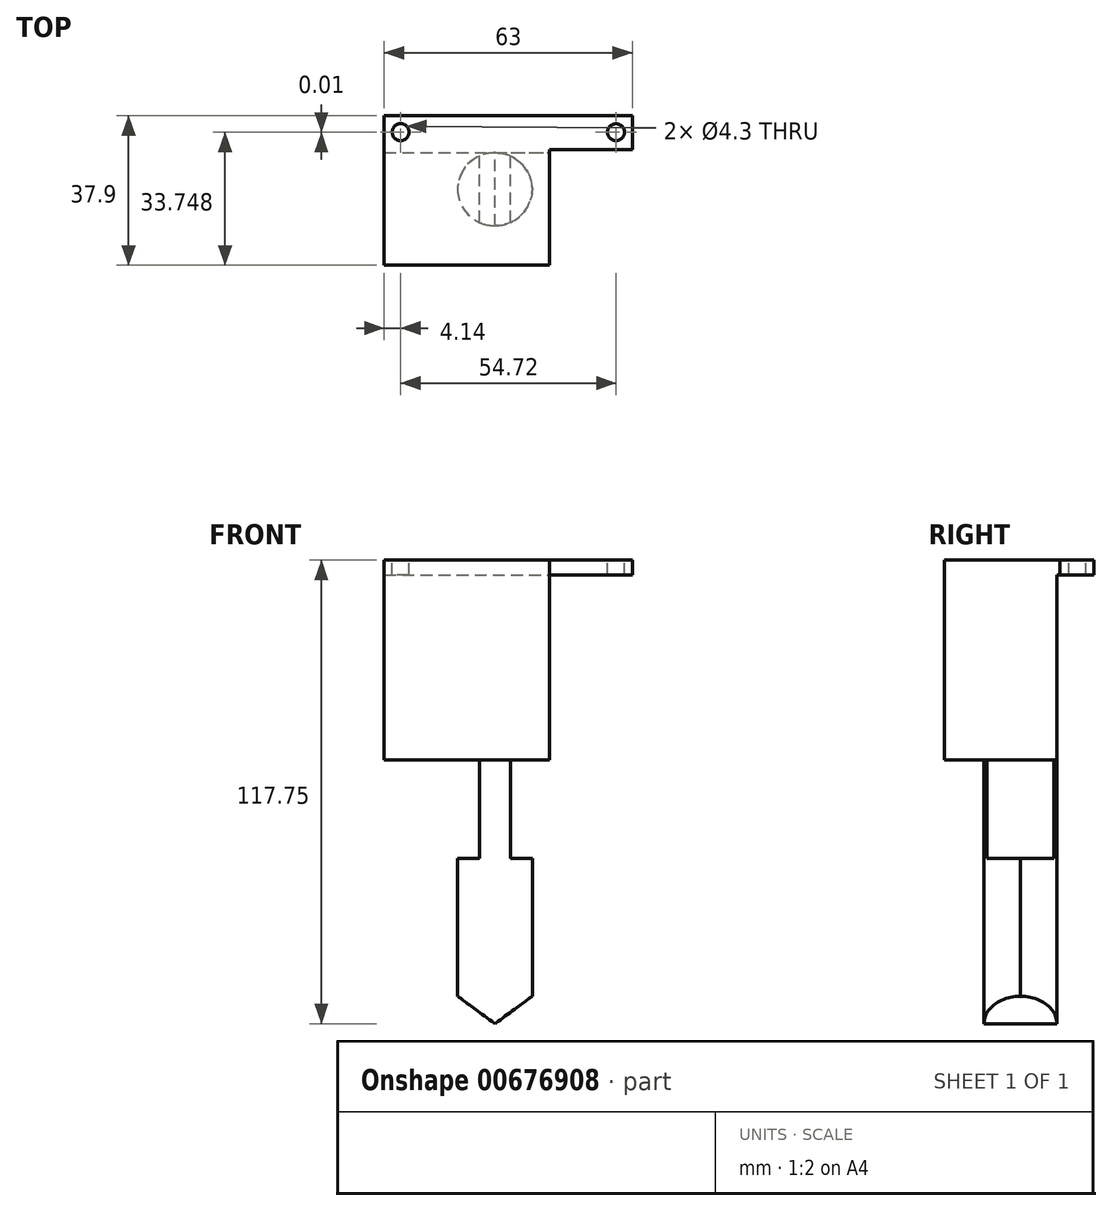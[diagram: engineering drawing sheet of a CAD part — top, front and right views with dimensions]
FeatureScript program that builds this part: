
annotation { "Feature Type Name" : "Feature", "Feature Type Description" : "" }
export const myFeature = defineFeature(function(context is Context, id is Id, definition is map)
    precondition{}
    {
        {
            var Q0;
            Q0=qCreatedBy(makeId("Front.planeOp"),FACE);
            var sketch = newSketch(context, id + "F0", { "sketchPlane" : qUnion([Q0])});
            skLineSegment(sketch, "E0", {"start": v(9.5, 7) * mm, "end": v(0, 0) * mm});
            skLineSegment(sketch, "E1", {"start": v(9.5, 7) * mm, "end": v(9.5, 42) * mm});
            skLineSegment(sketch, "E2", {"start": v(9.5, 42) * mm, "end": v(3.9, 42) * mm});
            skLineSegment(sketch, "E3", {"start": v(3.9, 42) * mm, "end": v(3.9, 67) * mm});
            skLineSegment(sketch, "E4", {"start": v(3.9, 67) * mm, "end": v(13.9, 67) * mm});
            skLineSegment(sketch, "E5", {"start": v(13.9, 67) * mm, "end": v(13.9, 114) * mm});
            skLineSegment(sketch, "E6", {"start": v(13.9, 114) * mm, "end": v(34.9, 114) * mm});
            skLineSegment(sketch, "E7", {"start": v(34.9, 114) * mm, "end": v(34.9, 117.75) * mm});
            skLineSegment(sketch, "E8", {"start": v(34.9, 117.75) * mm, "end": v(-28.1, 117.75) * mm});
            skLineSegment(sketch, "E9", {"start": v(-28.1, 117.75) * mm, "end": v(-28.1, 114) * mm});
            skLineSegment(sketch, "E10", {"start": v(-28.1, 114) * mm, "end": v(-28.1, 67) * mm});
            skLineSegment(sketch, "E11", {"start": v(-28.1, 67) * mm, "end": v(-3.9, 67) * mm});
            skLineSegment(sketch, "E12", {"start": v(-3.9, 67) * mm, "end": v(-3.9, 42) * mm});
            skLineSegment(sketch, "E13", {"start": v(-3.9, 42) * mm, "end": v(-9.5, 42) * mm});
            skLineSegment(sketch, "E14", {"start": v(-9.5, 42) * mm, "end": v(-9.5, 7) * mm});
            skLineSegment(sketch, "E15", {"start": v(-9.5, 7) * mm, "end": v(0, 0) * mm});
            skSolve(sketch);
        }
        {
            var Q0;
            Q0=makeQuery(id+"F0.imprint","IMPRINT",FACE,{"disambiguationData":[TD([[makeQuery(id+"F0.imprint","IMPRINT",EDGE,{"derivedFrom":sQuery(id+"F0.wireOp",EDGE,"E0")}),-1.0]])]});
            extrude(context, id + "F1", {"entities" : qUnion([Q0]), "depth" : 18.5 / 2 * mm, "offsetDistance" : 25.4 * mm, "hasSecondDirection" : true, "secondDirectionOppositeDirection" : true, "secondDirectionDepth" : 18.5 / 2 * mm});
        }
        {
            var Q0;
            Q0=makeQuery(id+"F1.opExtrude","CAP_FACE",FACE,{"disambiguationData":[OSD([sQuery(id+"F0.wireOp",EDGE,"E0"),sQuery(id+"F0.wireOp",EDGE,"E1"),sQuery(id+"F0.wireOp",EDGE,"E2"),sQuery(id+"F0.wireOp",EDGE,"E3"),sQuery(id+"F0.wireOp",EDGE,"E4"),sQuery(id+"F0.wireOp",EDGE,"E5"),sQuery(id+"F0.wireOp",EDGE,"E6"),sQuery(id+"F0.wireOp",EDGE,"E7"),sQuery(id+"F0.wireOp",EDGE,"E8"),sQuery(id+"F0.wireOp",EDGE,"E9"),sQuery(id+"F0.wireOp",EDGE,"E10"),sQuery(id+"F0.wireOp",EDGE,"E11"),sQuery(id+"F0.wireOp",EDGE,"E12"),sQuery(id+"F0.wireOp",EDGE,"E13"),sQuery(id+"F0.wireOp",EDGE,"E14"),sQuery(id+"F0.wireOp",EDGE,"E15")])],"isStart":false});
            var sketch = newSketch(context, id + "F2", { "sketchPlane" : qUnion([Q0])});
            skLineSegment(sketch, "E16.bottom", {"start": v(13.9, 67) * mm, "end": v(-28.1, 67) * mm});
            skLineSegment(sketch, "E16.top", {"start": v(13.9, 117.75) * mm, "end": v(-28.1, 117.75) * mm});
            skLineSegment(sketch, "E16.left", {"start": v(13.9, 67) * mm, "end": v(13.9, 117.75) * mm});
            skLineSegment(sketch, "E16.right", {"start": v(-28.1, 67) * mm, "end": v(-28.1, 117.75) * mm});
            skSolve(sketch);
        }
        {
            var Q0;
            {var subQ0=sQuery(id+"F2.wireOp",EDGE,"E16.top");Q0=makeQuery(id+"F2.imprint","IMPRINT",FACE,{"disambiguationData":[TD([[makeQuery(id+"F2.imprint","IMPRINT",EDGE,{"derivedFrom":subQ0}),1.0]])]});}
            extrude(context, id + "F3", {"entities" : qUnion([Q0]), "operationType" : NewBodyOperationType.ADD, "depth" : 10 * mm, "offsetDistance" : 25.4 * mm});
        }
        {
            var Q0;
            Q0=makeQuery(id+"F1.opExtrude","CAP_FACE",FACE,{"disambiguationData":[OSD([sQuery(id+"F0.wireOp",EDGE,"E0"),sQuery(id+"F0.wireOp",EDGE,"E1"),sQuery(id+"F0.wireOp",EDGE,"E2"),sQuery(id+"F0.wireOp",EDGE,"E3"),sQuery(id+"F0.wireOp",EDGE,"E4"),sQuery(id+"F0.wireOp",EDGE,"E5"),sQuery(id+"F0.wireOp",EDGE,"E6"),sQuery(id+"F0.wireOp",EDGE,"E7"),sQuery(id+"F0.wireOp",EDGE,"E8"),sQuery(id+"F0.wireOp",EDGE,"E9"),sQuery(id+"F0.wireOp",EDGE,"E10"),sQuery(id+"F0.wireOp",EDGE,"E11"),sQuery(id+"F0.wireOp",EDGE,"E12"),sQuery(id+"F0.wireOp",EDGE,"E13"),sQuery(id+"F0.wireOp",EDGE,"E14"),sQuery(id+"F0.wireOp",EDGE,"E15")])],"isStart":true});
            var sketch = newSketch(context, id + "F4", { "sketchPlane" : qUnion([Q0])});
            skLineSegment(sketch, "E17.bottom", {"start": v(-34.9, 114) * mm, "end": v(28.1, 114) * mm});
            skLineSegment(sketch, "E17.top", {"start": v(-34.9, 117.75) * mm, "end": v(28.1, 117.75) * mm});
            skLineSegment(sketch, "E17.left", {"start": v(-34.9, 114) * mm, "end": v(-34.9, 117.75) * mm});
            skLineSegment(sketch, "E17.right", {"start": v(28.1, 114) * mm, "end": v(28.1, 117.75) * mm});
            skSolve(sketch);
        }
        {
            var Q0;
            Q0=makeQuery(id+"F4.imprint","IMPRINT",FACE,{"disambiguationData":[TD([[makeQuery(id+"F4.imprint","IMPRINT",EDGE,{"derivedFrom":sQuery(id+"F4.wireOp",EDGE,"E17.top")}),-1.0]])]});
            extrude(context, id + "F5", {"entities" : qUnion([Q0]), "operationType" : NewBodyOperationType.ADD, "depth" : 9.4 * mm, "offsetDistance" : 25.4 * mm});
        }
        {
            var Q0;
            Q0=makeQuery(id+"F5.boolean.opBoolean","MERGE",FACE,{"derivedFrom":[makeQuery(id+"F3.boolean.opBoolean","MERGE",FACE,{"derivedFrom":[makeQuery(id+"F1.opExtrude","SWEPT_FACE",FACE,{"disambiguationData":[OSD([sQuery(id+"F0.wireOp",EDGE,"E8")])]}),makeQuery(id+"F3.opExtrude","SWEPT_FACE",FACE,{"disambiguationData":[OSD([sQuery(id+"F2.wireOp",EDGE,"E16.top")])]})]}),makeQuery(id+"F5.opExtrude","SWEPT_FACE",FACE,{"disambiguationData":[OSD([sQuery(id+"F4.wireOp",EDGE,"E17.top")])]})]});
            var sketch = newSketch(context, id + "F6", { "sketchPlane" : qUnion([Q0])});
            skCircle(sketch, "E18", {"center": v(30.76, 14.5) * mm, "radius": 2.15 * mm});
            skCircle(sketch, "E19", {"center": v(-23.96, 14.5) * mm, "radius": 2.15 * mm});
            skSolve(sketch);
        }
        {
            var Q0;
            Q0=makeQuery(id+"F6.imprint","IMPRINT",FACE,{"disambiguationData":[TD([[makeQuery(id+"F6.imprint","IMPRINT",EDGE,{"derivedFrom":sQuery(id+"F6.wireOp",EDGE,"E19")}),1.0]])]});
            var Q1;
            Q1=makeQuery(id+"F6.imprint","IMPRINT",FACE,{"disambiguationData":[TD([[makeQuery(id+"F6.imprint","IMPRINT",EDGE,{"derivedFrom":sQuery(id+"F6.wireOp",EDGE,"E18")}),1.0]])]});
            extrude(context, id + "F7", {"entities" : qUnion([Q0, Q1]), "operationType" : NewBodyOperationType.REMOVE, "endBound" : BoundingType.THROUGH_ALL, "oppositeDirection" : true, "depth" : 25.4 * mm, "offsetDistance" : 25.4 * mm});
        }
        {
            var Q0;
            {var subQ0=sQuery(id+"F0.wireOp",EDGE,"E8");var subQ1=sQuery(id+"F0.wireOp",EDGE,"E7");var subQ2=sQuery(id+"F0.wireOp",EDGE,"E6");var subQ3=sQuery(id+"F0.wireOp",EDGE,"E5");Q0=makeQuery(id+"F3.boolean.opBoolean","SPLIT",FACE,{"disambiguationData":[TD([makeQuery(id+"F1.opExtrude","SWEPT_FACE",FACE,{"disambiguationData":[OSD([subQ3])]})])],"derivedFrom":makeQuery(id+"F1.opExtrude","CAP_FACE",FACE,{"disambiguationData":[OSD([sQuery(id+"F0.wireOp",EDGE,"E0"),sQuery(id+"F0.wireOp",EDGE,"E1"),sQuery(id+"F0.wireOp",EDGE,"E2"),sQuery(id+"F0.wireOp",EDGE,"E3"),sQuery(id+"F0.wireOp",EDGE,"E4"),subQ3,subQ2,subQ1,subQ0,sQuery(id+"F0.wireOp",EDGE,"E9"),sQuery(id+"F0.wireOp",EDGE,"E10"),sQuery(id+"F0.wireOp",EDGE,"E11"),sQuery(id+"F0.wireOp",EDGE,"E12"),sQuery(id+"F0.wireOp",EDGE,"E13"),sQuery(id+"F0.wireOp",EDGE,"E14"),sQuery(id+"F0.wireOp",EDGE,"E15")])],"isStart":false})});}
            var sketch = newSketch(context, id + "F8", { "sketchPlane" : qUnion([Q0])});
            skLineSegment(sketch, "E20.bottom", {"start": v(34.9, 117.75) * mm, "end": v(13.9, 117.75) * mm});
            skLineSegment(sketch, "E20.top", {"start": v(34.9, 114) * mm, "end": v(13.9, 114) * mm});
            skLineSegment(sketch, "E20.left", {"start": v(34.9, 117.75) * mm, "end": v(34.9, 114) * mm});
            skLineSegment(sketch, "E20.right", {"start": v(13.9, 117.75) * mm, "end": v(13.9, 114) * mm});
            skSolve(sketch);
        }
        {
            var Q0;
            Q0=makeQuery(id+"F8.imprint","IMPRINT",FACE,{"disambiguationData":[TD([[makeQuery(id+"F8.imprint","IMPRINT",EDGE,{"derivedFrom":sQuery(id+"F8.wireOp",EDGE,"E20.bottom")}),1.0]])]});
            extrude(context, id + "F9", {"entities" : qUnion([Q0]), "operationType" : NewBodyOperationType.REMOVE, "oppositeDirection" : true, "depth" : 19.3 * mm, "offsetDistance" : 25.4 * mm});
        }
        {
            var Q0;
            Q0=makeQuery(id+"F1.opExtrude","CAP_EDGE",EDGE,{"disambiguationData":[OSD([sQuery(id+"F0.wireOp",EDGE,"E1")])],"isStart":false});
            var Q1;
            Q1=makeQuery(id+"F1.opExtrude","CAP_EDGE",EDGE,{"disambiguationData":[OSD([sQuery(id+"F0.wireOp",EDGE,"E1")])],"isStart":true});
            var Q2;
            Q2=makeQuery(id+"F1.opExtrude","CAP_EDGE",EDGE,{"disambiguationData":[OSD([sQuery(id+"F0.wireOp",EDGE,"E14")])],"isStart":true});
            var Q3;
            Q3=makeQuery(id+"F1.opExtrude","CAP_EDGE",EDGE,{"disambiguationData":[OSD([sQuery(id+"F0.wireOp",EDGE,"E14")])],"isStart":false});
            fillet(context, id + "F10", {"entities" : qUnion([Q0, Q1, Q2, Q3]), "radius" : 9.4 * mm, "tangentPropagation" : true, "allowEdgeOverflow" : false});
        }
    });
